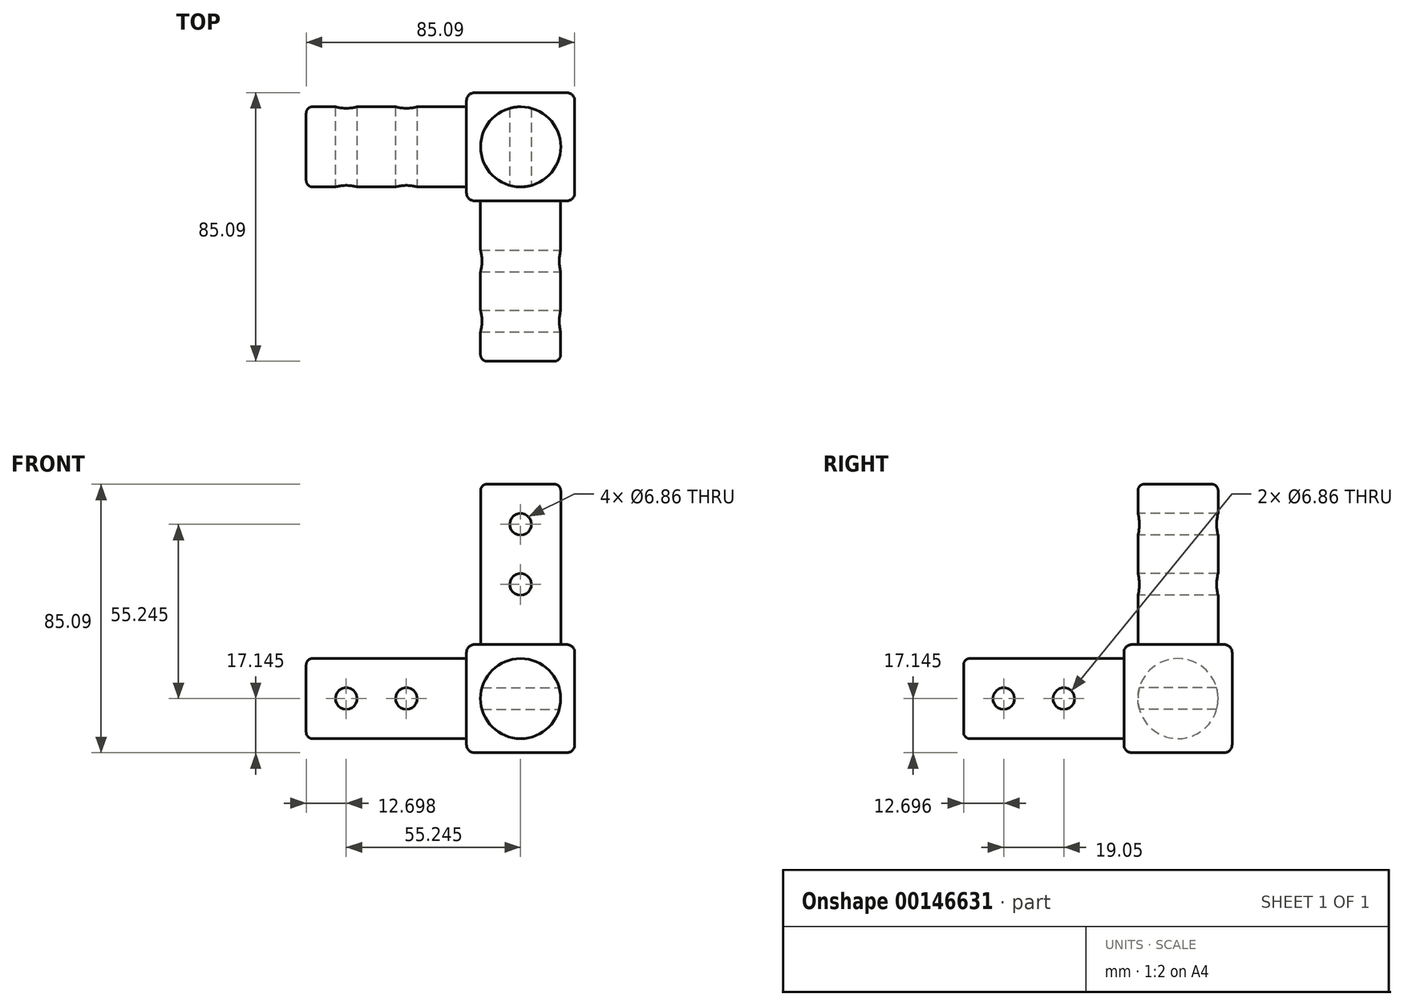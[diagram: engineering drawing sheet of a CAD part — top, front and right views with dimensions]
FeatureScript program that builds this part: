
annotation { "Feature Type Name" : "Feature", "Feature Type Description" : "" }
export const myFeature = defineFeature(function(context is Context, id is Id, definition is map)
    precondition{}
    {
        {
            var Q0;
            Q0=qCreatedBy(makeId("Top.planeOp"),FACE);
            var sketch = newSketch(context, id + "F0", { "sketchPlane" : qUnion([Q0])});
            skLineSegment(sketch, "E0.bottom", {"start": v(-13.47, 23.7) * mm, "end": v(20.82, 23.7) * mm});
            skLineSegment(sketch, "E0.top", {"start": v(-13.47, -10.58) * mm, "end": v(20.82, -10.58) * mm});
            skLineSegment(sketch, "E0.left", {"start": v(-13.47, 23.7) * mm, "end": v(-13.47, -10.58) * mm});
            skLineSegment(sketch, "E0.right", {"start": v(20.82, 23.7) * mm, "end": v(20.82, -10.58) * mm});
            skSolve(sketch);
        }
        {
            var Q0;
            Q0 = qSketchRegion(id + "F0", true);
            extrude(context, id + "F1", {"entities" : qUnion([Q0]), "depth" : 34.3 * mm});
        }
        {
            var Q0;
            Q0=makeQuery(id+"F1.opExtrude","CAP_FACE",FACE,{"disambiguationData":[OSD([sQuery(id+"F0.wireOp",EDGE,"E0.bottom"),sQuery(id+"F0.wireOp",EDGE,"E0.top"),sQuery(id+"F0.wireOp",EDGE,"E0.left"),sQuery(id+"F0.wireOp",EDGE,"E0.right")])],"isStart":false});
            var sketch = newSketch(context, id + "F2", { "sketchPlane" : qUnion([Q0])});
            skCircle(sketch, "E1", {"center": v(3.68, 6.56) * mm, "radius": 12.7 * mm});
            skLineSegment(sketch, "E2", {"start": v(3.67, 23.7) * mm, "end": v(3.67, -12.79) * mm, "construction": true});
            skLineSegment(sketch, "E3", {"start": v(20.82, 6.56) * mm, "end": v(-13.47, 6.56) * mm, "construction": true});
            skSolve(sketch);
        }
        {
            var Q0;
            Q0 = qSketchRegion(id + "F2", true);
            extrude(context, id + "F3", {"entities" : qUnion([Q0]), "operationType" : NewBodyOperationType.ADD, "depth" : 50.8 * mm});
        }
        {
            var Q0;
            Q0=makeQuery(id+"F1.opExtrude","SWEPT_FACE",FACE,{"disambiguationData":[OSD([sQuery(id+"F0.wireOp",EDGE,"E0.left")])]});
            var sketch = newSketch(context, id + "F4", { "sketchPlane" : qUnion([Q0])});
            skLineSegment(sketch, "E4", {"start": v(-23.7, 17.15) * mm, "end": v(13.45, 17.15) * mm, "construction": true});
            skLineSegment(sketch, "E5", {"start": v(-6.56, 0) * mm, "end": v(-6.56, 34.3) * mm, "construction": true});
            skCircle(sketch, "E6", {"center": v(-6.56, 17.15) * mm, "radius": 12.7 * mm});
            skSolve(sketch);
        }
        {
            var Q0;
            Q0 = qSketchRegion(id + "F4", true);
            extrude(context, id + "F5", {"entities" : qUnion([Q0]), "operationType" : NewBodyOperationType.ADD, "depth" : 50.8 * mm});
        }
        {
            var Q0;
            Q0=makeQuery(id+"F1.opExtrude","SWEPT_FACE",FACE,{"disambiguationData":[OSD([sQuery(id+"F0.wireOp",EDGE,"E0.top")])]});
            var sketch = newSketch(context, id + "F6", { "sketchPlane" : qUnion([Q0])});
            skLineSegment(sketch, "E7", {"start": v(-13.47, 17.15) * mm, "end": v(24.43, 17.15) * mm, "construction": true});
            skLineSegment(sketch, "E8", {"start": v(3.67, 0) * mm, "end": v(3.67, 34.3) * mm, "construction": true});
            skCircle(sketch, "E9", {"center": v(3.67, 17.15) * mm, "radius": 12.7 * mm});
            skSolve(sketch);
        }
        {
            var Q0;
            Q0 = qSketchRegion(id + "F6", true);
            extrude(context, id + "F7", {"entities" : qUnion([Q0]), "operationType" : NewBodyOperationType.ADD, "depth" : 50.8 * mm});
        }
        {
            var Q0;
            Q0=qCreatedBy(makeId("Front.planeOp"),FACE);
            var sketch = newSketch(context, id + "F8", { "sketchPlane" : qUnion([Q0])});
            skCircle(sketch, "E10", {"center": v(3.67, 53.34) * mm, "radius": 3.43 * mm});
            skCircle(sketch, "E11", {"center": v(3.67, 72.4) * mm, "radius": 3.43 * mm});
            skSolve(sketch);
        }
        {
            var Q0;
            Q0 = qSketchRegion(id + "F8", true);
            extrude(context, id + "F9", {"entities" : qUnion([Q0]), "operationType" : NewBodyOperationType.REMOVE, "endBound" : BoundingType.SYMMETRIC, "oppositeDirection" : true, "depth" : 50.8 * mm});
        }
        {
            var Q0;
            Q0=qCreatedBy(makeId("Right.planeOp"),FACE);
            var sketch = newSketch(context, id + "F10", { "sketchPlane" : qUnion([Q0])});
            skCircle(sketch, "E12", {"center": v(-29.63, 17.15) * mm, "radius": 3.43 * mm});
            skCircle(sketch, "E13", {"center": v(-48.68, 17.15) * mm, "radius": 3.43 * mm});
            skSolve(sketch);
        }
        {
            var Q0;
            Q0 = qSketchRegion(id + "F10", true);
            extrude(context, id + "F11", {"entities" : qUnion([Q0]), "operationType" : NewBodyOperationType.REMOVE, "endBound" : BoundingType.SYMMETRIC, "oppositeDirection" : true, "depth" : 50.8 * mm});
        }
        {
            var Q0;
            Q0=qCreatedBy(makeId("Front.planeOp"),FACE);
            var sketch = newSketch(context, id + "F12", { "sketchPlane" : qUnion([Q0])});
            skCircle(sketch, "E14", {"center": v(-51.57, 17.15) * mm, "radius": 3.43 * mm});
            skCircle(sketch, "E15", {"center": v(-32.52, 17.15) * mm, "radius": 3.43 * mm});
            skSolve(sketch);
        }
        {
            var Q0;
            Q0 = qSketchRegion(id + "F12", true);
            extrude(context, id + "F13", {"entities" : qUnion([Q0]), "operationType" : NewBodyOperationType.REMOVE, "endBound" : BoundingType.SYMMETRIC, "oppositeDirection" : true, "depth" : 50.8 * mm});
        }
        {
            var Q0;
            Q0=makeQuery(id+"F3.opExtrude","CAP_EDGE",EDGE,{"disambiguationData":[OSD([sQuery(id+"F2.wireOp",EDGE,"E1")])],"isStart":false});
            var Q1;
            Q1=makeQuery(id+"F7.opExtrude","CAP_EDGE",EDGE,{"disambiguationData":[OSD([sQuery(id+"F6.wireOp",EDGE,"E9")])],"isStart":false});
            var Q2;
            Q2=makeQuery(id+"F5.opExtrude","CAP_EDGE",EDGE,{"disambiguationData":[OSD([sQuery(id+"F4.wireOp",EDGE,"E6")])],"isStart":false});
            fillet(context, id + "F14", {"entities" : qUnion([Q0, Q1, Q2]), "radius" : 2.03 * mm, "tangentPropagation" : true, "allowEdgeOverflow" : false});
        }
        {
            var Q0;
            Q0=makeQuery(id+"F1.opExtrude","SWEPT_EDGE",EDGE,{"disambiguationData":[OSD([sQuery(id+"F0.wireOp",EDGE,"E0.bottom"),sQuery(id+"F0.wireOp",EDGE,"E0.right")])]});
            var Q1;
            Q1=makeQuery(id+"F1.opExtrude","CAP_EDGE",EDGE,{"disambiguationData":[OSD([sQuery(id+"F0.wireOp",EDGE,"E0.right")])],"isStart":false});
            var Q2;
            Q2=makeQuery(id+"F1.opExtrude","SWEPT_EDGE",EDGE,{"disambiguationData":[OSD([sQuery(id+"F0.wireOp",EDGE,"E0.top"),sQuery(id+"F0.wireOp",EDGE,"E0.right")])]});
            var Q3;
            Q3=makeQuery(id+"F1.opExtrude","CAP_EDGE",EDGE,{"disambiguationData":[OSD([sQuery(id+"F0.wireOp",EDGE,"E0.right")])],"isStart":true});
            var Q4;
            Q4=makeQuery(id+"F1.opExtrude","CAP_EDGE",EDGE,{"disambiguationData":[OSD([sQuery(id+"F0.wireOp",EDGE,"E0.bottom")])],"isStart":true});
            var Q5;
            Q5=makeQuery(id+"F1.opExtrude","CAP_EDGE",EDGE,{"disambiguationData":[OSD([sQuery(id+"F0.wireOp",EDGE,"E0.bottom")])],"isStart":false});
            var Q6;
            Q6=makeQuery(id+"F1.opExtrude","SWEPT_EDGE",EDGE,{"disambiguationData":[OSD([sQuery(id+"F0.wireOp",EDGE,"E0.bottom"),sQuery(id+"F0.wireOp",EDGE,"E0.left")])]});
            var Q7;
            Q7=makeQuery(id+"F1.opExtrude","CAP_EDGE",EDGE,{"disambiguationData":[OSD([sQuery(id+"F0.wireOp",EDGE,"E0.left")])],"isStart":true});
            var Q8;
            Q8=makeQuery(id+"F1.opExtrude","CAP_EDGE",EDGE,{"disambiguationData":[OSD([sQuery(id+"F0.wireOp",EDGE,"E0.top")])],"isStart":true});
            var Q9;
            Q9=makeQuery(id+"F1.opExtrude","CAP_EDGE",EDGE,{"disambiguationData":[OSD([sQuery(id+"F0.wireOp",EDGE,"E0.left")])],"isStart":false});
            var Q10;
            Q10=makeQuery(id+"F1.opExtrude","SWEPT_EDGE",EDGE,{"disambiguationData":[OSD([sQuery(id+"F0.wireOp",EDGE,"E0.top"),sQuery(id+"F0.wireOp",EDGE,"E0.left")])]});
            var Q11;
            Q11=makeQuery(id+"F1.opExtrude","CAP_EDGE",EDGE,{"disambiguationData":[OSD([sQuery(id+"F0.wireOp",EDGE,"E0.top")])],"isStart":false});
            fillet(context, id + "F15", {"entities" : qUnion([Q0, Q1, Q2, Q3, Q4, Q5, Q6, Q7, Q8, Q9, Q10, Q11]), "radius" : 2.54 * mm, "tangentPropagation" : true, "allowEdgeOverflow" : false});
        }
    });
